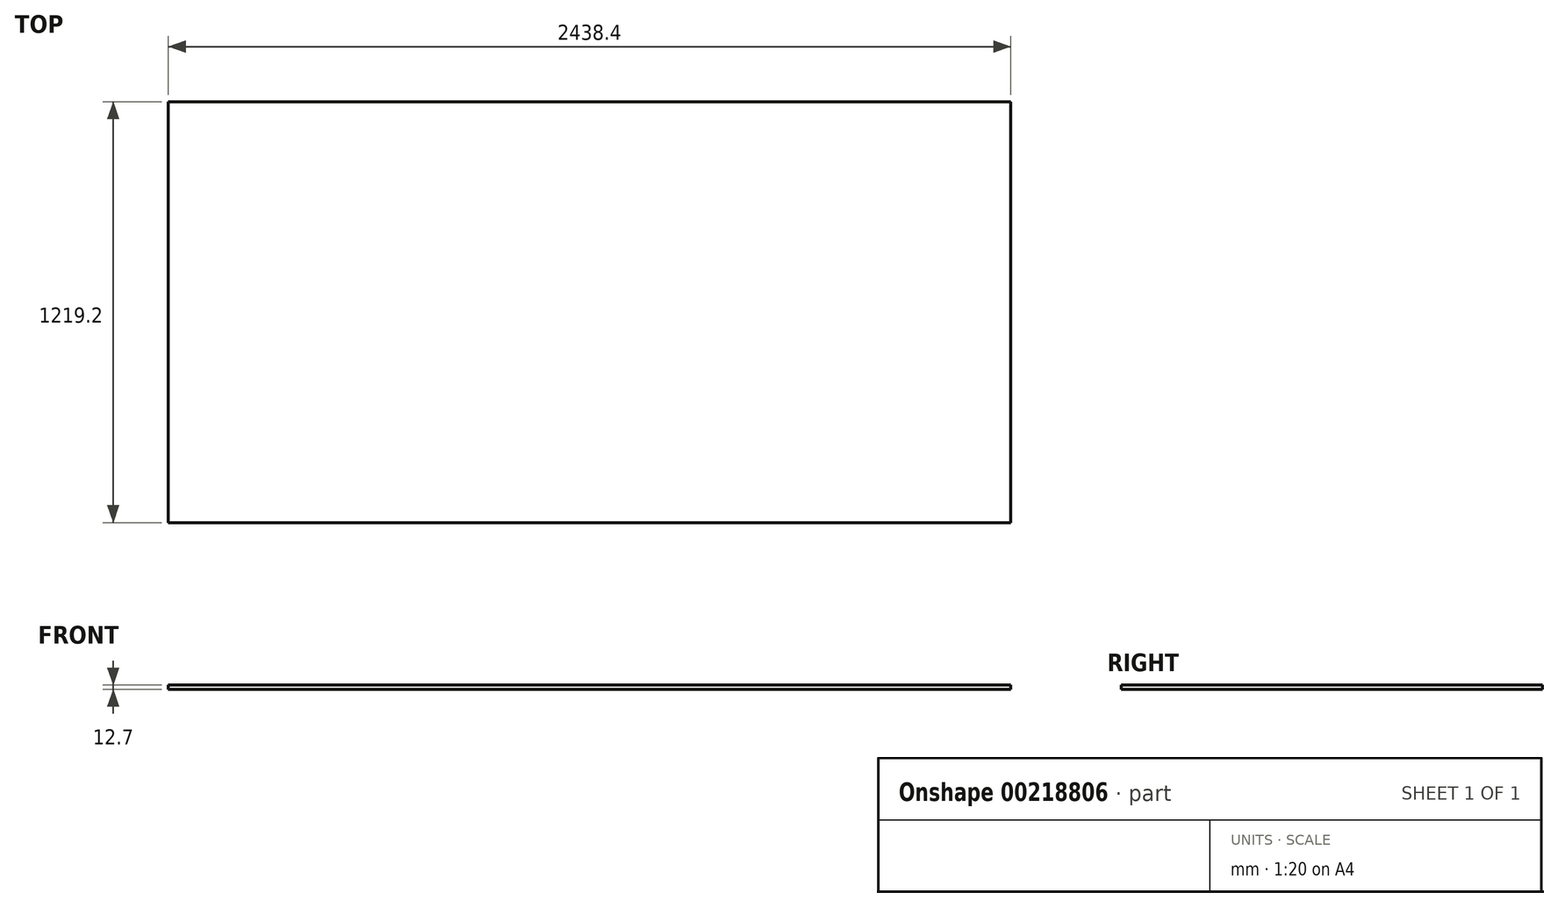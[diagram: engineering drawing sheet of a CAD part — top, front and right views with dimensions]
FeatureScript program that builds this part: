
annotation { "Feature Type Name" : "Feature", "Feature Type Description" : "" }
export const myFeature = defineFeature(function(context is Context, id is Id, definition is map)
    precondition{}
    {
        {
            var Q0;
            Q0=qCreatedBy(makeId("Top.planeOp"),FACE);
            var sketch = newSketch(context, id + "F0", { "sketchPlane" : qUnion([Q0])});
            skLineSegment(sketch, "E0.bottom", {"start": v(0, 0) * mm, "end": v(2438.4, 0) * mm});
            skLineSegment(sketch, "E0.top", {"start": v(0, -1219.2) * mm, "end": v(2438.4, -1219.2) * mm});
            skLineSegment(sketch, "E0.left", {"start": v(0, 0) * mm, "end": v(0, -1219.2) * mm});
            skLineSegment(sketch, "E0.right", {"start": v(2438.4, 0) * mm, "end": v(2438.4, -1219.2) * mm});
            skSolve(sketch);
        }
        {
            var Q0;
            Q0=makeQuery(id+"F0.imprint","IMPRINT",FACE,{"disambiguationData":[TD([[makeQuery(id+"F0.imprint","IMPRINT",EDGE,{"derivedFrom":sQuery(id+"F0.wireOp",EDGE,"E0.bottom")}),-1.0]])]});
            extrude(context, id + "F1", {"entities" : qUnion([Q0]), "depth" : 12.7 * mm});
        }
    });
